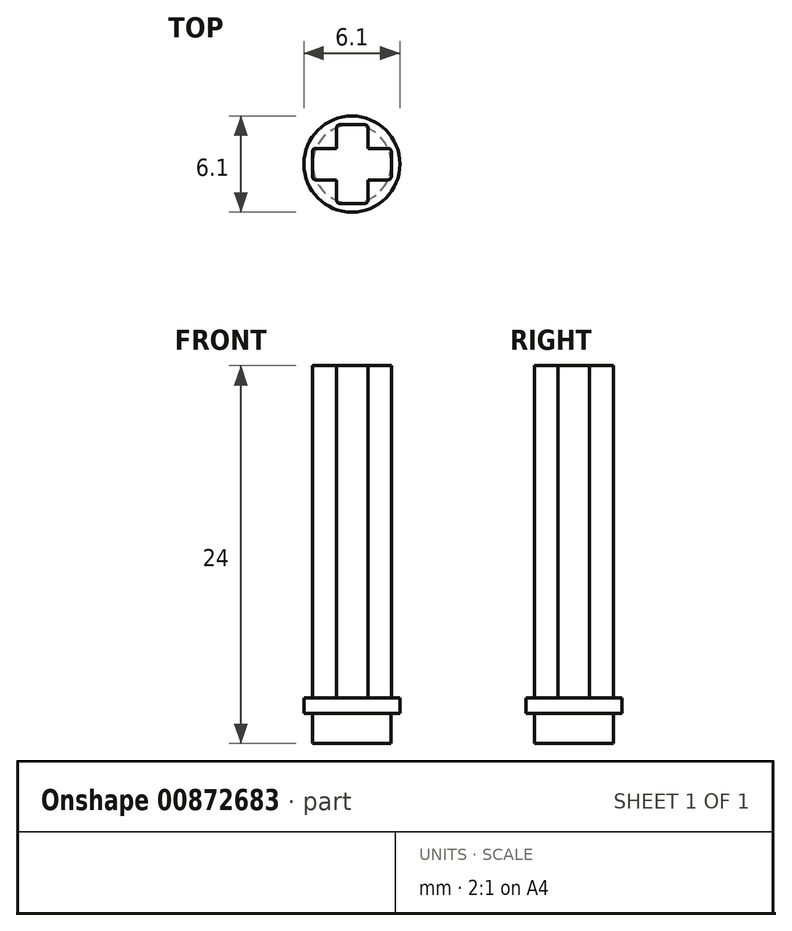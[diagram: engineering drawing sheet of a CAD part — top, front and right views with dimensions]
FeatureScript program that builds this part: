
annotation { "Feature Type Name" : "Feature", "Feature Type Description" : "" }
export const myFeature = defineFeature(function(context is Context, id is Id, definition is map)
    precondition{}
    {
        {
            var Q0;
            Q0=qCreatedBy(makeId("Top.planeOp"),FACE);
            var sketch = newSketch(context, id + "F0", { "sketchPlane" : qUnion([Q0])});
            skLineSegment(sketch, "E0.bottom", {"start": v(-17.82, 22.13) * mm, "end": v(-12.82, 22.13) * mm});
            skLineSegment(sketch, "E0.top", {"start": v(-17.82, 20.13) * mm, "end": v(-12.82, 20.13) * mm});
            skLineSegment(sketch, "E0.left", {"start": v(-17.82, 22.13) * mm, "end": v(-17.82, 20.13) * mm});
            skLineSegment(sketch, "E0.right", {"start": v(-12.82, 22.13) * mm, "end": v(-12.82, 20.13) * mm});
            skLineSegment(sketch, "E1.bottom", {"start": v(-16.3, 23.63) * mm, "end": v(-14.3, 23.63) * mm});
            skLineSegment(sketch, "E1.top", {"start": v(-16.3, 18.63) * mm, "end": v(-14.3, 18.63) * mm});
            skLineSegment(sketch, "E1.left", {"start": v(-16.3, 23.63) * mm, "end": v(-16.3, 18.63) * mm});
            skLineSegment(sketch, "E1.right", {"start": v(-14.3, 23.63) * mm, "end": v(-14.3, 18.63) * mm});
            skSolve(sketch);
        }
        {
            var Q0;
            Q0=qSketchRegion(id+"F0",true);
            extrude(context, id + "F1", {"entities" : qUnion([Q0]), "depth" : 21.1 * mm, "offsetDistance" : 25 * mm});
        }
        {
            var Q0;
            Q0=qCreatedBy(makeId("Top.planeOp"),FACE);
            var sketch = newSketch(context, id + "F2", { "sketchPlane" : qUnion([Q0])});
            skCircle(sketch, "E2", {"center": v(-15.32, 21.13) * mm, "radius": 3.05 * mm});
            skSolve(sketch);
        }
        {
            var Q0;
            Q0=makeQuery(id+"F2.imprint","IMPRINT",FACE,{"disambiguationData":[TD([[makeQuery(id+"F2.imprint","IMPRINT",EDGE,{"derivedFrom":sQuery(id+"F2.wireOp",EDGE,"E2")}),1.0]])]});
            extrude(context, id + "F3", {"entities" : qUnion([Q0]), "operationType" : NewBodyOperationType.ADD, "oppositeDirection" : true, "depth" : 1 * mm, "offsetDistance" : 25 * mm});
        }
        {
            var Q0;
            Q0=makeQuery(id+"F3.opExtrude","CAP_FACE",FACE,{"disambiguationData":[OSD([sQuery(id+"F2.wireOp",EDGE,"E2")])],"isStart":false});
            var sketch = newSketch(context, id + "F4", { "sketchPlane" : qUnion([Q0])});
            skCircle(sketch, "E3", {"center": v(-15.32, -21.13) * mm, "radius": 2.5 * mm});
            skSolve(sketch);
        }
        {
            var Q0;
            Q0=qSketchRegion(id+"F4",true);
            extrude(context, id + "F5", {"entities" : qUnion([Q0]), "operationType" : NewBodyOperationType.ADD, "depth" : 1.9 * mm, "offsetDistance" : 25 * mm});
        }
        {
            var Q0;
            Q0=makeQuery(id+"F1.opExtrude","SWEPT_EDGE",EDGE,{"disambiguationData":[OSD([sQuery(id+"F0.wireOp",EDGE,"E0.top"),sQuery(id+"F0.wireOp",EDGE,"E0.right")])]});
            var Q1;
            Q1=makeQuery(id+"F1.opExtrude","SWEPT_EDGE",EDGE,{"disambiguationData":[OSD([sQuery(id+"F0.wireOp",EDGE,"E0.bottom"),sQuery(id+"F0.wireOp",EDGE,"E0.right")])]});
            var Q2;
            Q2=makeQuery(id+"F1.opExtrude","SWEPT_EDGE",EDGE,{"disambiguationData":[OSD([sQuery(id+"F0.wireOp",EDGE,"E1.top"),sQuery(id+"F0.wireOp",EDGE,"E1.right")])]});
            var Q3;
            Q3=makeQuery(id+"F1.opExtrude","SWEPT_EDGE",EDGE,{"disambiguationData":[OSD([sQuery(id+"F0.wireOp",EDGE,"E1.top"),sQuery(id+"F0.wireOp",EDGE,"E1.left")])]});
            var Q4;
            Q4=makeQuery(id+"F1.opExtrude","SWEPT_EDGE",EDGE,{"disambiguationData":[OSD([sQuery(id+"F0.wireOp",EDGE,"E0.top"),sQuery(id+"F0.wireOp",EDGE,"E0.left")])]});
            var Q5;
            Q5=makeQuery(id+"F1.opExtrude","SWEPT_EDGE",EDGE,{"disambiguationData":[OSD([sQuery(id+"F0.wireOp",EDGE,"E0.bottom"),sQuery(id+"F0.wireOp",EDGE,"E0.left")])]});
            var Q6;
            Q6=makeQuery(id+"F1.opExtrude","SWEPT_EDGE",EDGE,{"disambiguationData":[OSD([sQuery(id+"F0.wireOp",EDGE,"E1.bottom"),sQuery(id+"F0.wireOp",EDGE,"E1.left")])]});
            var Q7;
            Q7=makeQuery(id+"F1.opExtrude","SWEPT_EDGE",EDGE,{"disambiguationData":[OSD([sQuery(id+"F0.wireOp",EDGE,"E1.bottom"),sQuery(id+"F0.wireOp",EDGE,"E1.right")])]});
            fillet(context, id + "F6", {"entities" : qUnion([Q0, Q1, Q2, Q3, Q4, Q5, Q6, Q7]), "radius" : 0.2 * mm, "tangentPropagation" : true, "allowEdgeOverflow" : false});
        }
    });
